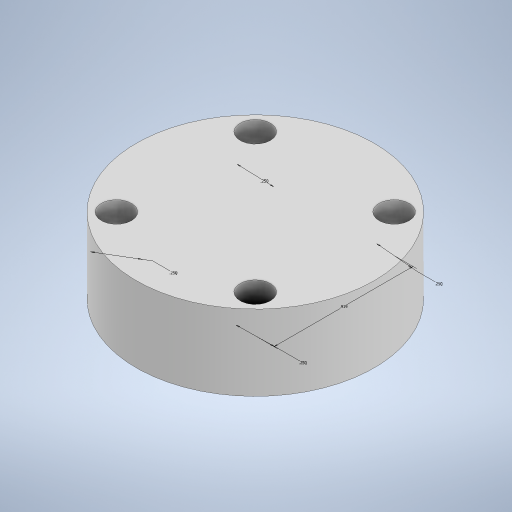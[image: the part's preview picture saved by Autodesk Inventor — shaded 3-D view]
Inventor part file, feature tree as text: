
AUTODESK INVENTOR PART (.ipt)
format: ipt  version: 2023 (Build 270158000, 158)  size: 264,704 bytes
history: native  units: in
note: dims shown in document units (in); Inventor stores cm internally (conversion verified against a paired STEP export)
features: sketch x5, extrude x4
ambient origin geometry x8: Origin, YZ Plane, XZ Plane, XY Plane, X Axis, Y Axis, Z Axis, Center Point
bodies: Solid1 (feature_tree)
feature tree (9):
  extrude  "Extrusion1"  Depth=0.919in
  extrude  "Extrusion2"  Depth=0.098in
  sketch  "Sketch5"  dims[d4=0.098in d5=0.098in]
  sketch  "Sketch6"  dims[d6=0.098in d7=0.25in d8=0.0in]
  extrude  "Extrusion3"  Depth=0.098in
  extrude  "Extrusion4"  Depth=0.25in TaperAngle=0.0deg
  sketch  "Sketch1"  dims[d0=1.575in d1=0.919in]
  sketch  "Sketch3"  dims[d2=0.919in d3=0.098in]
  sketch  "Sketch7"  dims[d10=0.125in d11=0.25in d12=0.0in d13=0.919in d14=0.25in d15=0.25in d16=0.25in d17=0.25in d18=0.25in d19=0.0in d20=0.919in d21=0.919in d22=0.2in d23=0.2in d24=0.2in d25=0.2in d26=0.25in d27=0.0in]
